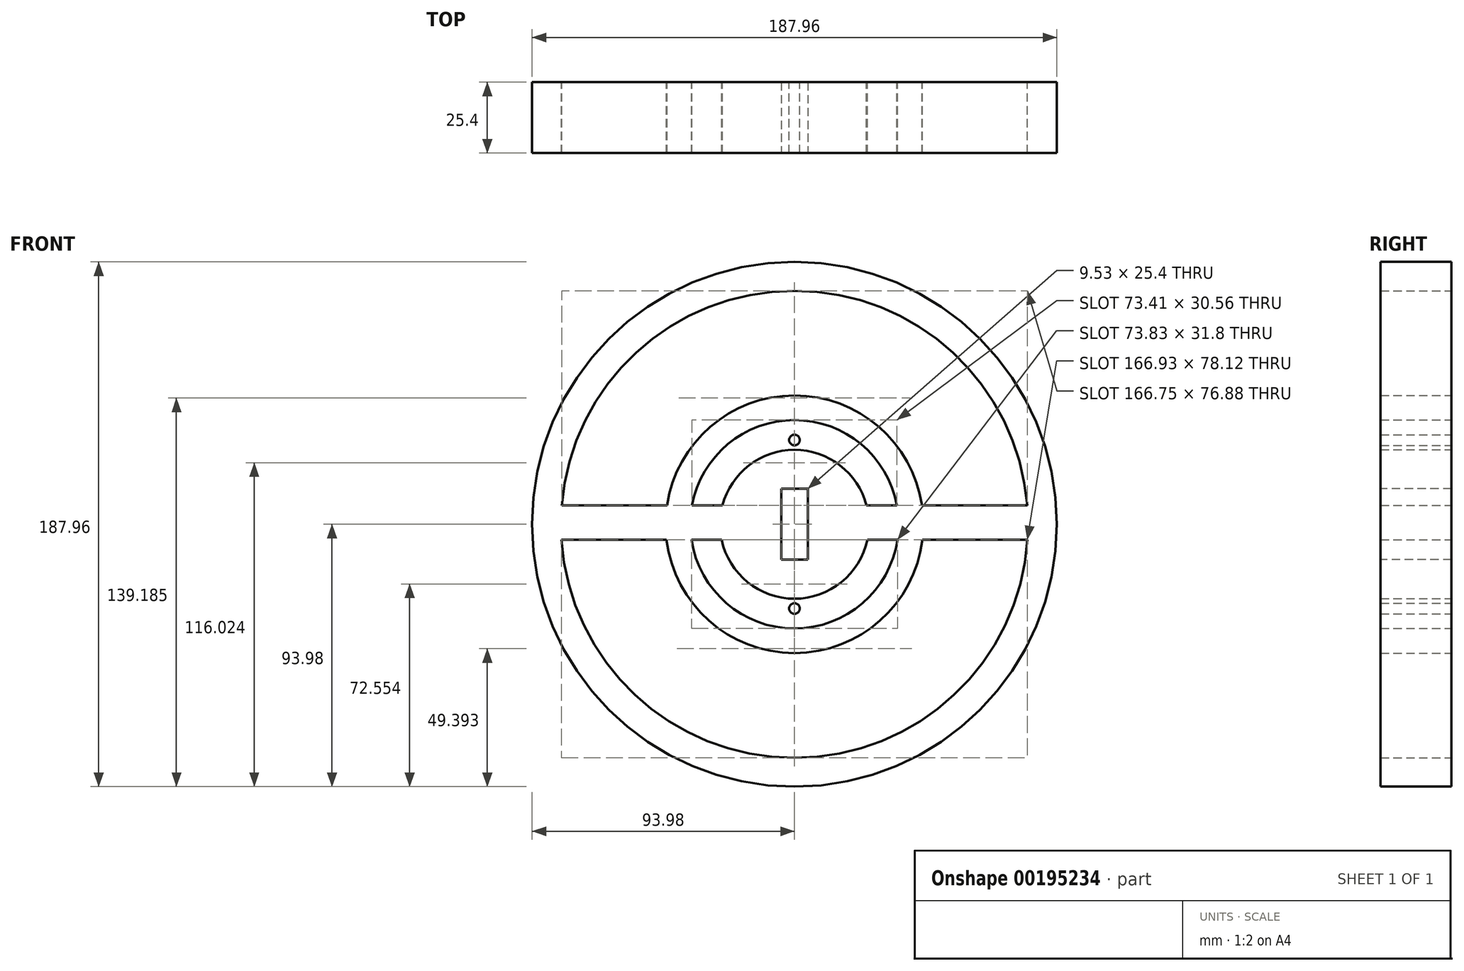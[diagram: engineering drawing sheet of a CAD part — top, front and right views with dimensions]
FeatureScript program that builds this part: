
annotation { "Feature Type Name" : "Feature", "Feature Type Description" : "" }
export const myFeature = defineFeature(function(context is Context, id is Id, definition is map)
    precondition{}
    {
        {
            var Q0;
            Q0=qCreatedBy(makeId("Front.planeOp"),FACE);
            var sketch = newSketch(context, id + "F0", { "sketchPlane" : qUnion([Q0])});
            skLineSegment(sketch, "E0.bottom", {"start": v(-4.76, 12.7) * mm, "end": v(4.76, 12.7) * mm});
            skLineSegment(sketch, "E0.top", {"start": v(-4.76, -12.7) * mm, "end": v(4.76, -12.7) * mm});
            skLineSegment(sketch, "E0.left", {"start": v(-4.76, 12.7) * mm, "end": v(-4.76, -12.7) * mm});
            skLineSegment(sketch, "E0.right", {"start": v(4.76, 12.7) * mm, "end": v(4.76, -12.7) * mm});
            skCircle(sketch, "E1", {"center": v(0, -30.18) * mm, "radius": 1.9 * mm});
            skCircle(sketch, "E2", {"center": v(0, 30.18) * mm, "radius": 1.9 * mm});
            skCircle(sketch, "E3", {"center": v(0, 0) * mm, "radius": 93.98 * mm});
            skArc(sketch, "E4", {"start": v(-36.91, -5.53) * mm, "mid": v(0, -37.32) * mm, "end": v(36.91, -5.53) * mm});
            skArc(sketch, "E5", {"start": v(-83.46, -5.53) * mm, "mid": v(0, -83.65) * mm, "end": v(83.46, -5.53) * mm});
            skArc(sketch, "E6", {"start": v(45.64, 6.76) * mm, "mid": v(0, 46.14) * mm, "end": v(-45.64, 6.76) * mm});
            skLineSegment(sketch, "E7", {"start": v(-83.37, 6.76) * mm, "end": v(-45.64, 6.76) * mm});
            skLineSegment(sketch, "E8", {"start": v(-83.46, -5.53) * mm, "end": v(-45.81, -5.53) * mm});
            skLineSegment(sketch, "E9", {"start": v(45.81, -5.53) * mm, "end": v(83.46, -5.53) * mm});
            skPoint(sketch, "E9.startSnap0", {"position": v(-60.19, -5.53) * mm});
            skLineSegment(sketch, "E10", {"start": v(45.64, 6.76) * mm, "end": v(83.37, 6.76) * mm});
            skPoint(sketch, "E11.orphan", {"position": v(-36.7, 6.76) * mm});
            skPoint(sketch, "E12.orphan", {"position": v(-36.91, -5.53) * mm});
            skArc(sketch, "E13.trimOffspring", {"start": v(83.37, 6.76) * mm, "mid": v(0, 83.65) * mm, "end": v(-83.37, 6.76) * mm});
            skArc(sketch, "E14.trimOffspring", {"start": v(-45.81, -5.53) * mm, "mid": v(0, -46.14) * mm, "end": v(45.81, -5.53) * mm});
            skPoint(sketch, "E15.orphan", {"position": v(0, -50.8) * mm});
            skPoint(sketch, "E16.orphan", {"position": v(-30.37, 0) * mm});
            skArc(sketch, "E17", {"start": v(-26.1, -5.53) * mm, "mid": v(0, -26.67) * mm, "end": v(26.1, -5.53) * mm});
            skArc(sketch, "E18", {"start": v(-22.18, -5.53) * mm, "mid": v(0, -22.86) * mm, "end": v(22.18, -5.53) * mm});
            skLineSegment(sketch, "E19", {"start": v(-36.7, 6.76) * mm, "end": v(-25.8, 6.76) * mm});
            skLineSegment(sketch, "E20", {"start": v(-36.91, -5.53) * mm, "end": v(-26.1, -5.53) * mm});
            skLineSegment(sketch, "E21", {"start": v(45.64, 6.76) * mm, "end": v(25.8, 6.76) * mm});
            skLineSegment(sketch, "E22", {"start": v(45.81, -5.53) * mm, "end": v(26.1, -5.53) * mm});
            skArc(sketch, "E23.trimOffspring", {"start": v(21.84, 6.76) * mm, "mid": v(0, 22.86) * mm, "end": v(-21.84, 6.76) * mm});
            skArc(sketch, "E24.trimOffspring", {"start": v(25.8, 6.76) * mm, "mid": v(0, 26.67) * mm, "end": v(-25.8, 6.76) * mm});
            skArc(sketch, "E25.trimOffspring", {"start": v(36.7, 6.76) * mm, "mid": v(0, 37.32) * mm, "end": v(-36.7, 6.76) * mm});
            skSolve(sketch);
        }
        {
            var Q0;
            Q0=makeQuery(id+"F0.imprint","IMPRINT",FACE,{"disambiguationData":[TD([[makeQuery(id+"F0.imprint","IMPRINT",EDGE,{"derivedFrom":sQuery(id+"F0.wireOp",EDGE,"E3")}),1.0]])]});
            var Q1;
            Q1=makeQuery(id+"F0.imprint","IMPRINT",FACE,{"disambiguationData":[TD([[makeQuery(id+"F0.imprint","IMPRINT",EDGE,{"derivedFrom":sQuery(id+"F0.wireOp",EDGE,"E2")}),1.0]])]});
            var Q2;
            Q2=makeQuery(id+"F0.imprint","IMPRINT",FACE,{"disambiguationData":[TD([[makeQuery(id+"F0.imprint","IMPRINT",EDGE,{"derivedFrom":sQuery(id+"F0.wireOp",EDGE,"E0.bottom")}),-1.0]])]});
            var Q3;
            Q3=makeQuery(id+"F0.imprint","IMPRINT",FACE,{"disambiguationData":[TD([[makeQuery(id+"F0.imprint","IMPRINT",EDGE,{"derivedFrom":sQuery(id+"F0.wireOp",EDGE,"E1")}),1.0]])]});
            var Q4;
            Q4=makeQuery(id+"F0.imprint","IMPRINT",FACE,{"disambiguationData":[TD([[makeQuery(id+"F0.imprint","IMPRINT",EDGE,{"derivedFrom":sQuery(id+"F0.wireOp",EDGE,"E0.bottom")}),1.0]])]});
            extrude(context, id + "F1", {"entities" : qUnion([Q0, Q1, Q2, Q3, Q4]), "depth" : 25.4 * mm});
        }
        {
            var Q0;
            Q0=qCreatedBy(makeId("Front.planeOp"),FACE);
            var sketch = newSketch(context, id + "F2", { "sketchPlane" : qUnion([Q0])});
            skLineSegment(sketch, "E26.bottom", {"start": v(4.76, 12.7) * mm, "end": v(-4.76, 12.7) * mm});
            skLineSegment(sketch, "E26.top", {"start": v(4.76, -12.7) * mm, "end": v(-4.76, -12.7) * mm});
            skLineSegment(sketch, "E26.left", {"start": v(4.76, 12.7) * mm, "end": v(4.76, -12.7) * mm});
            skLineSegment(sketch, "E26.right", {"start": v(-4.76, 12.7) * mm, "end": v(-4.76, -12.7) * mm});
            skPoint(sketch, "E26.middle", {"position": v(0, 0) * mm});
            skCircle(sketch, "E27", {"center": v(0, 32.08) * mm, "radius": 1.9 * mm});
            skCircle(sketch, "E28", {"center": v(0, -32.08) * mm, "radius": 1.9 * mm});
            skSolve(sketch);
        }
        {
            var Q0;
            Q0=makeQuery(id+"F1.opExtrude","CAP_FACE",FACE,{"disambiguationData":[OSD([sQuery(id+"F0.wireOp",EDGE,"E3"),sQuery(id+"F0.wireOp",EDGE,"E5"),sQuery(id+"F0.wireOp",EDGE,"E6"),sQuery(id+"F0.wireOp",EDGE,"E7"),sQuery(id+"F0.wireOp",EDGE,"E8"),sQuery(id+"F0.wireOp",EDGE,"E9"),sQuery(id+"F0.wireOp",EDGE,"E10"),sQuery(id+"F0.wireOp",EDGE,"E13.trimOffspring"),sQuery(id+"F0.wireOp",EDGE,"E14.trimOffspring")])],"isStart":false});
            var sketch = newSketch(context, id + "F3", { "sketchPlane" : qUnion([Q0])});
            skCircle(sketch, "E29", {"center": v(0, 0) * mm, "radius": 22.86 * mm});
            skCircle(sketch, "E30", {"center": v(0, 0) * mm, "radius": 26.67 * mm});
            skSolve(sketch);
        }
        {
            var Q0;
            Q0 = qSketchRegion(id + "F2", true);
            var Q1;
            Q1 = qSketchRegion(id + "F3", true);
            extrude(context, id + "F4", {"entities" : qUnion([Q0, Q1]), "operationType" : NewBodyOperationType.REMOVE, "oppositeDirection" : true, "depth" : 25.4 * mm});
        }
        {
            var Q0;
            Q0=makeQuery(id+"F4.boolean.opBoolean","SPLIT",FACE,{"disambiguationData":[TD([makeQuery(id+"F4.opExtrude","SWEPT_FACE",FACE,{"disambiguationData":[OSD([sQuery(id+"F3.wireOp",EDGE,"E29")])]})])],"derivedFrom":makeQuery(id+"F1.opExtrude","CAP_FACE",FACE,{"disambiguationData":[OSD([sQuery(id+"F0.wireOp",EDGE,"E3"),sQuery(id+"F0.wireOp",EDGE,"E5"),sQuery(id+"F0.wireOp",EDGE,"E6"),sQuery(id+"F0.wireOp",EDGE,"E7"),sQuery(id+"F0.wireOp",EDGE,"E8"),sQuery(id+"F0.wireOp",EDGE,"E9"),sQuery(id+"F0.wireOp",EDGE,"E10"),sQuery(id+"F0.wireOp",EDGE,"E13.trimOffspring"),sQuery(id+"F0.wireOp",EDGE,"E14.trimOffspring")])],"isStart":false})});
            var sketch = newSketch(context, id + "F5", { "sketchPlane" : qUnion([Q0])});
            skLineSegment(sketch, "E31.bottom", {"start": v(4.76, 12.7) * mm, "end": v(-4.76, 12.7) * mm});
            skLineSegment(sketch, "E31.top", {"start": v(4.76, -12.7) * mm, "end": v(-4.76, -12.7) * mm});
            skLineSegment(sketch, "E31.left", {"start": v(4.76, 12.7) * mm, "end": v(4.76, -12.7) * mm});
            skLineSegment(sketch, "E31.right", {"start": v(-4.76, 12.7) * mm, "end": v(-4.76, -12.7) * mm});
            skPoint(sketch, "E31.middle", {"position": v(0, 0) * mm});
            skSolve(sketch);
        }
        {
            var Q0;
            Q0 = qSketchRegion(id + "F5", true);
            extrude(context, id + "F6", {"entities" : qUnion([Q0]), "operationType" : NewBodyOperationType.REMOVE, "endBound" : BoundingType.THROUGH_ALL, "oppositeDirection" : true, "depth" : 25.4 * mm});
        }
        {
            var Q0;
            Q0 = qSketchRegion(id + "F0", true);
            extrude(context, id + "F7", {"entities" : qUnion([Q0]), "operationType" : NewBodyOperationType.ADD, "depth" : 25.4 * mm});
        }
    });
